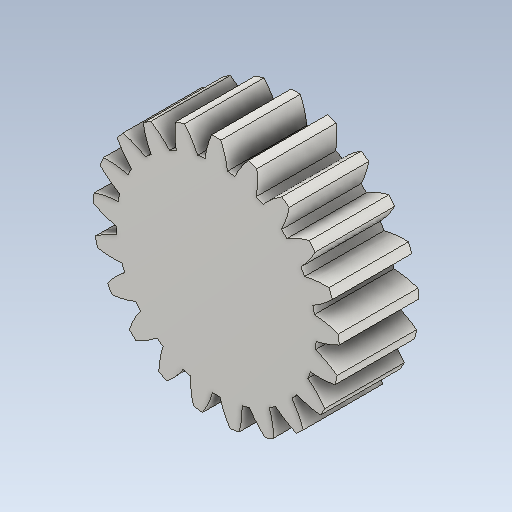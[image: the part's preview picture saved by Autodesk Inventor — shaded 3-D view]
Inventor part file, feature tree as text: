
AUTODESK INVENTOR PART (.ipt)
format: ipt  version: 2020 (Build 240168000, 168)  size: 258,048 bytes
history: native  units: mm (DEFAULTED — no unit token found)
features: plane x3, other x3, sketch x2, extrude x1
ambient origin geometry x8: Origin, YZ Plane, XZ Plane, XY Plane, X Axis, Y Axis, Z Axis, Center Point
bodies: Solid1 (feature_tree)
feature tree (9):
  extrude  "Extrusion1"  Depth=7.6mm TaperAngle=0.0deg
  plane  "Work Plane2"
  plane  "Work Plane8"
  plane  "Work Plane9"
  other  "Przekładnia walcowa"
  sketch  "Sketch1"  dims[d0=23.512079mm d1=7.6mm d2=0.0mm]
  sketch  "Sketch2"  dims[d3=21.552986mm d4=10.0mm d5=0.0mm d16=19.500321mm d17=0.0mm d34=1.495997mm d39=0.0mm d41=0.0mm d43=19.500321mm d46=19.500321mm d47=0.0mm d48=0.0mm]
  other  "Srf1"
  other  "Średnica podziałowa"
